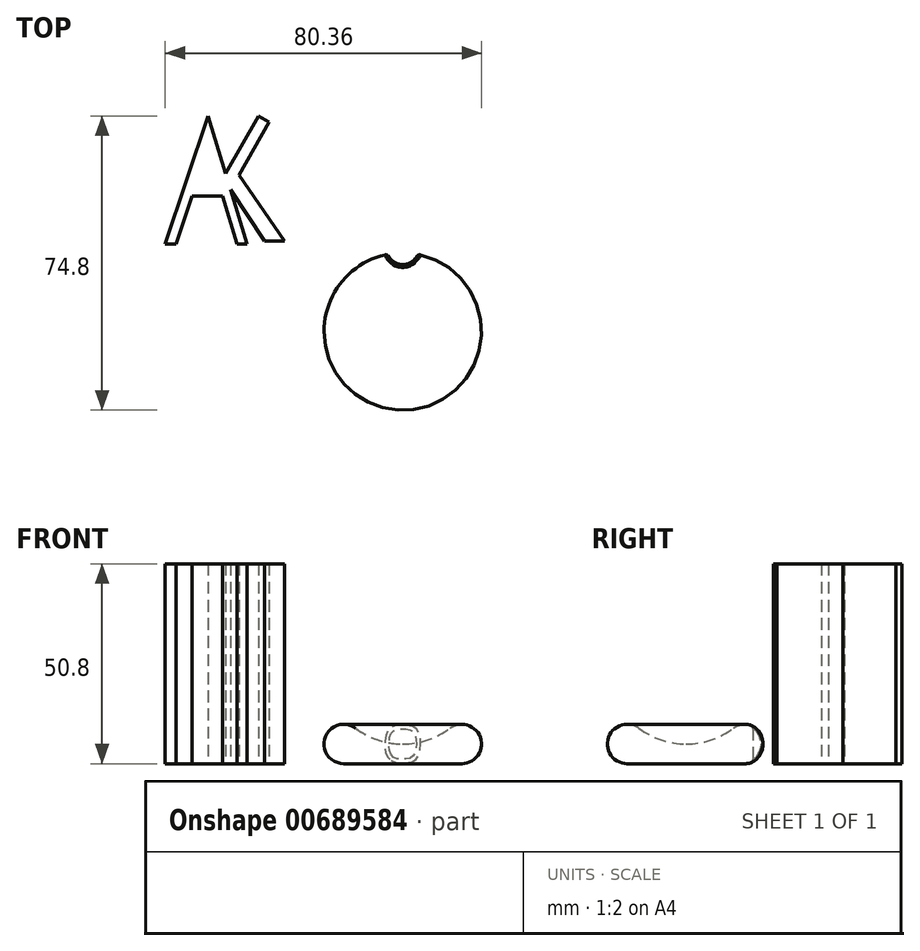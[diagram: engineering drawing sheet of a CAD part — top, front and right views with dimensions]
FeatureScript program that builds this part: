
annotation { "Feature Type Name" : "Feature", "Feature Type Description" : "" }
export const myFeature = defineFeature(function(context is Context, id is Id, definition is map)
    precondition{}
    {
        {
            var Q0;
            Q0=qCreatedBy(makeId("Front.planeOp"),FACE);
            var sketch = newSketch(context, id + "F0", { "sketchPlane" : qUnion([Q0])});
            skArc(sketch, "E0", {"start": v(-12, 9) * mm, "mid": v(-19.74, 6.58) * mm, "end": v(-15, 0) * mm});
            skArc(sketch, "E1", {"start": v(-12, 9) * mm, "mid": v(-6.32, 6.03) * mm, "end": v(0, 5) * mm});
            skLineSegment(sketch, "E2", {"start": v(-15, 0) * mm, "end": v(0, 0) * mm});
            skLineSegment(sketch, "E3", {"start": v(0, 0) * mm, "end": v(0, 5) * mm});
            skPoint(sketch, "E4.orphan", {"position": v(-9.4, 0) * mm});
            skSolve(sketch);
        }
        {
            var Q0;
            Q0=makeQuery(id+"F0.imprint","IMPRINT",FACE,{"disambiguationData":[TD([[makeQuery(id+"F0.imprint","IMPRINT",EDGE,{"derivedFrom":sQuery(id+"F0.wireOp",EDGE,"E0")}),1.0]])]});
            var Q1;
            Q1=sQuery(id+"F0.wireOp",EDGE,"E3");
            revolve(context, id + "F1", {"entities" : qUnion([Q0]), "axis" : qUnion([Q1]), "revolveType" : RevolveType.FULL});
        }
        {
            var Q0;
            Q0=qCreatedBy(makeId("Top.planeOp"),FACE);
            var sketch = newSketch(context, id + "F2", { "sketchPlane" : qUnion([Q0])});
            skCircle(sketch, "E5", {"center": v(0, 21) * mm, "radius": 4 * mm});
            skSolve(sketch);
        }
        {
            var Q0;
            Q0=makeQuery(id+"F2.imprint","IMPRINT",FACE,{"disambiguationData":[TD([[makeQuery(id+"F2.imprint","IMPRINT",EDGE,{"derivedFrom":sQuery(id+"F2.wireOp",EDGE,"E5")}),1.0]])]});
            extrude(context, id + "F3", {"entities" : qUnion([Q0]), "operationType" : NewBodyOperationType.REMOVE, "depth" : 25 * mm, "offsetDistance" : 25.4 * mm});
        }
        {
            var Q0;
            Q0=makeQuery(id+"F3.boolean.opBoolean","INTERSECT",EDGE,{"derivedFrom":[makeQuery(id+"F1.opRevolve","SWEPT_FACE",FACE,{"disambiguationData":[OSD([sQuery(id+"F0.wireOp",EDGE,"E0")])]}),makeQuery(id+"F3.opExtrude","SWEPT_FACE",FACE,{"disambiguationData":[OSD([sQuery(id+"F2.wireOp",EDGE,"E5")])]})]});
            fillet(context, id + "F4", {"entities" : qUnion([Q0]), "radius" : 1 * mm, "tangentPropagation" : true, "allowEdgeOverflow" : false});
        }
        {
            var Q0;
            Q0=qCreatedBy(makeId("Top.planeOp"),FACE);
            var sketch = newSketch(context, id + "F5", { "sketchPlane" : qUnion([Q0])});
            skLineSegment(sketch, "E6", {"start": v(-49.42, 46.51) * mm, "end": v(-42.04, 22.24) * mm});
            skLineSegment(sketch, "E7", {"start": v(-49.42, 46.51) * mm, "end": v(-57.58, 22.24) * mm});
            skLineSegment(sketch, "E8", {"start": v(-45.73, 34.37) * mm, "end": v(-53.5, 34.37) * mm});
            skLineSegment(sketch, "E9", {"start": v(-49.42, 46.51) * mm, "end": v(-51.93, 47.35) * mm});
            skLineSegment(sketch, "E10", {"start": v(-51.93, 47.35) * mm, "end": v(-60.36, 22.24) * mm});
            skLineSegment(sketch, "E11", {"start": v(-60.36, 22.24) * mm, "end": v(-57.58, 22.24) * mm});
            skLineSegment(sketch, "E12", {"start": v(-51.93, 47.35) * mm, "end": v(-49.42, 54.8) * mm});
            skLineSegment(sketch, "E13", {"start": v(-49.42, 54.8) * mm, "end": v(-46.9, 46.51) * mm});
            skLineSegment(sketch, "E14", {"start": v(-46.9, 46.51) * mm, "end": v(-39.53, 22.24) * mm});
            skLineSegment(sketch, "E15", {"start": v(-39.53, 22.24) * mm, "end": v(-42.04, 22.24) * mm});
            skLineSegment(sketch, "E16", {"start": v(-44.97, 40.16) * mm, "end": v(-36.6, 54.8) * mm});
            skLineSegment(sketch, "E17", {"start": v(-36.6, 54.8) * mm, "end": v(-33.92, 53.26) * mm});
            skLineSegment(sketch, "E18", {"start": v(-33.92, 53.26) * mm, "end": v(-41.6, 39.8) * mm});
            skLineSegment(sketch, "E19", {"start": v(-41.6, 39.8) * mm, "end": v(-30, 23.01) * mm});
            skLineSegment(sketch, "E20", {"start": v(-30, 23.01) * mm, "end": v(-35.05, 23.01) * mm});
            skLineSegment(sketch, "E21", {"start": v(-35.05, 23.01) * mm, "end": v(-43.74, 36.1) * mm});
            skLineSegment(sketch, "E22", {"start": v(-54.2, 32.27) * mm, "end": v(-45.1, 32.27) * mm});
            skSolve(sketch);
        }
        {
            var Q0;
            {var subQ3=sQuery(id+"F5.wireOp",EDGE,"E8");Q0=makeQuery(id+"F5.imprint","IMPRINT",FACE,{"disambiguationData":[TD([[makeQuery(id+"F5.imprint","IMPRINT",EDGE,{"derivedFrom":subQ3}),-1.0]])]});}
            var Q1;
            {var subQ0=sQuery(id+"F5.wireOp",EDGE,"E9");Q1=makeQuery(id+"F5.imprint","IMPRINT",FACE,{"disambiguationData":[TD([[makeQuery(id+"F5.imprint","IMPRINT",EDGE,{"derivedFrom":subQ0}),1.0]])]});}
            var Q2;
            {var subQ0=sQuery(id+"F5.wireOp",EDGE,"E16");Q2=makeQuery(id+"F5.imprint","IMPRINT",FACE,{"disambiguationData":[TD([[makeQuery(id+"F5.imprint","IMPRINT",EDGE,{"derivedFrom":subQ0}),-1.0]])]});}
            var Q3;
            {var subQ5=sQuery(id+"F5.wireOp",EDGE,"E9");Q3=makeQuery(id+"F5.imprint","IMPRINT",FACE,{"disambiguationData":[TD([[makeQuery(id+"F5.imprint","IMPRINT",EDGE,{"derivedFrom":subQ5}),-1.0]])]});}
            extrude(context, id + "F6", {"entities" : qUnion([Q0, Q1, Q2, Q3]), "depth" : 50.8 * mm, "offsetDistance" : 25.4 * mm});
        }
    });
